# Revit family: Doppelhalter VSG
name_source: partatom
category: HLS-Bauteile
revit_build: Autodesk Revit 2017 (Build: 20190507_1515(x64)
units: mm (PartAtom-declared; Revit-internal decimal feet)

## family parameters
Arbeitsebenenbasiert = Ja
Beim Laden mit Abzugskörper schneiden = Nein
Bemaßung runder Anschluss = Durchmesser verwenden
Gemeinsam genutzt = Ja
Immer vertikal = Nein
Raumberechnungspunkt = Nein
Teiletyp = Normal

## types (4) — shared parameters
Achsabstand = 46 - 154 mm
Fabrikat = MEFA
Firma = MEFA Befestigungs- und Montagesysteme GmbH
Kurztext1 = Doppelhalter VSG mit Gewindestift
Kurztext2 = Achsabstand L 46 - 154 mm
Lmax = 154 mm  [stored 0.505249 ft]
Lmin = 46 mm  [stored 0.150919 ft]
Länge = 180 mm  [stored 0.590551 ft]
Material = Stahl
Mengeneinheit = St
Vorgabe-Ansicht = 1219 mm
max. zul. Last Zug = 0.35 kN
vpe = 50 St
zero-valued in all types: Breite

## per-type parameters (varying)
| type | Artikelnummer | EAN | Gewicht | Gewicht pro Bauteil | Gewindestift | Gewindestifttyp | H | Höhe | L |
| Doppelhalter VSG, Gewindestift M 8x 20 | 0590118 | 4250928415080 | 0.12 kg | 0.12 kg | Gewindestifte : Gewindestift M8x20 | M8x20 | 20 mm  [stored 0.0656168 ft] | 20 mm | 80 mm  [stored 0.262467 ft] |
| Doppelhalter VSG, Gewindestift M 8x 30 | 0590126 | 4250928415097 | 0.13 kg | 0.13 kg | Gewindestifte : Gewindestift M8x30 | M8x30 | 30 mm  [stored 0.0984252 ft] | 30 mm | 80 mm  [stored 0.262467 ft] |
| Doppelhalter VSG, Gewindestift M 8x 40 | 0590134 | 4250928415103 | 0.14 kg | 0.14 kg | Gewindestifte : Gewindestift M8x40 | M8x40 | 40 mm  [stored 0.131234 ft] | 40 mm | 154 mm  [stored 0.505249 ft] |
| Doppelhalter VSG, Gewindestift M 8x 50 | 0590142 | 4250928415110 | 0.14 kg | 0.14 kg | Gewindestifte : Gewindestift M8x50 | M8x50 | 50 mm  [stored 0.164042 ft] | 50 mm | 154 mm  [stored 0.505249 ft] |

note: [stored X ft] marks values corroborated as IEEE doubles in the binary element streams (Revit-internal decimal feet)

## geometry (parser evidence)
native form markers: Sweep x2
no freeform markers — native parametric forms only
